# Revit family: Турникет тумбовый PERCo_TTD-03.1
name_source: partatom
category: Mechanical Equipment
units: mm (PartAtom-declared; Revit-internal decimal feet)

## family parameters
Always vertical = No
Classification = None
Cut with Voids When Loaded = No
Part Type = Normal
Room Calculation Point = No
Round Connector Dimension = Use Diameter
Shared = No
Work Plane-Based = No

## types (2) — shared parameters
Built-in reader = not provided
Card capture reader capacity = not provided
Current = 1 A
Dimensions = 1083×684×994 mm
Electrical connection = 220 B
IP Code = IP41
Manufacturer = PERCo
Maximum dimensions of ACS controller = max. 250×175×40 mm
Maximum dimensions of installed readers = 150×50×28 mm or 100×130×28 mm
Number = 1
Operating temperature = from +1°С to +50°С
Passageway width = 500 mm
Plank length = 511 mm
Rated power = 9 W
Throughput rate = 30 persons/min
URL = https://www.perco.com
Unit of measurement = pcs
Voltage = 12 V
Weight = max. 60 kg

## per-type parameters (varying)
| type | Frame | Full name | Lid | Material | Name |
| TTD-03.1S | Steel, stainless, polished | TTD-03.1S Electromechanical Box Tripod Turnstile for indoor application | Black stone | Housing ─ high-quality stainless steel. Top cover ─ stainless steel or radio-transparent artificial stone. Barrier arms ─ stainless steel. | TTD-03.1S Box tripod turnstile |
| TTD-03.1G | Powder coated steel | TTD-03.1G Electromechanical Box Tripod Turnstile for indoor application | Blue stone | Housing ─ powder-coated steel. Top cover ─ stainless steel or radio-transparent artificial stone. Barrier arms ─ stainless steel. | TTD-03.1G Box tripod turnstile |
